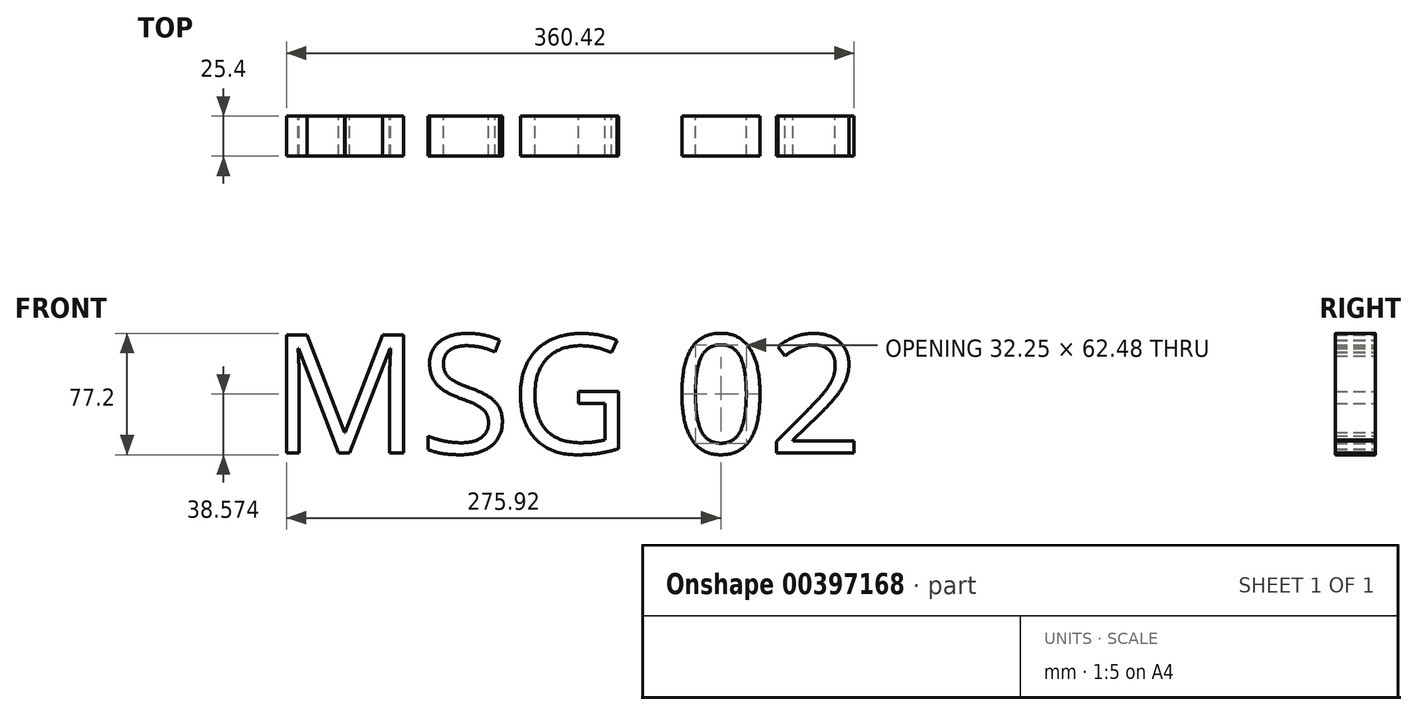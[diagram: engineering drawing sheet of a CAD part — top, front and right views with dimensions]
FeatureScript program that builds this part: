
annotation { "Feature Type Name" : "Feature", "Feature Type Description" : "" }
export const myFeature = defineFeature(function(context is Context, id is Id, definition is map)
    precondition{}
    {
        {
            var Q0;
            Q0=qCreatedBy(makeId("Front.planeOp"),FACE);
            var sketch = newSketch(context, id + "F0", { "sketchPlane" : qUnion([Q0])});
            skText(sketch, "E0", { "text": "MSG 02\n", "fontName": "OpenSans-Regular.ttf"});
            const initialGuessF0  = {"E0": [-0.12751, -0.0436, 1, 0, 0.07563]};
            skSetInitialGuess(sketch, initialGuessF0);
            skSolve(sketch);
        }
        {
            var Q0;
            Q0 = qSketchRegion(id + "F0", true);
            extrude(context, id + "F1", {"entities" : qUnion([Q0]), "depth" : 25.4 * mm});
        }
    });
